# Revit family: Installationskanal für System 55
name_source: partatom
category: Generic Models
revit_build: Autodesk Revit 2015 (Build: 20140606_1530(x64)
units: mm (PartAtom-declared; Revit-internal decimal feet)

## types (5) — shared parameters
Manufacturer = OBO Bettermann
Material = Steel, Galvanized
URL = http://www.obo-bettermann.com

## per-type parameters (varying)
| type | GTIN | Manufacturer Art. No. | Width |
| OKA-G20040140 | 4012195242925 | 7424000 | 200 mm  [stored 0.656168 ft] |
| OKA-G30040140 | 4012195242932 | 7424002 | 300 mm  [stored 0.984252 ft] |
| OKA-G40040140 | 4012195242949 | 7424004 | 400 mm  [stored 1.31234 ft] |
| OKA-G50040140 | 4012195242987 | 7424006 | 500 mm  [stored 1.64042 ft] |
| OKA-G60040140 | 4012195242994 | 7424008 | 600 mm |

note: column(s) folded — value = type name in every type: Article Type

note: [stored X ft] marks values corroborated as IEEE doubles in the binary element streams (Revit-internal decimal feet)

## geometry (parser evidence)
native form markers: Sweep x1
no freeform markers — native parametric forms only
